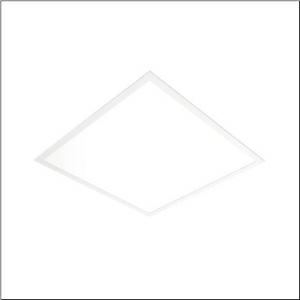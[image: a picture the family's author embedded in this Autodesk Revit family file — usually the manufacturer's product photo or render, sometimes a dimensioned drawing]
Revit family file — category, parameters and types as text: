
# Revit family: apollon_41_51mh12h72443
name_source: partatom
category: Lighting Fixtures
units: mm (PartAtom-declared; Revit-internal decimal feet)

## family parameters
Cut with Voids When Loaded = No
Host = Face
Light Source = No
Part Type = Normal
Room Calculation Point = No
Round Connector Dimension = Use Diameter
Shared = No

## types (1)
- Apollon 41 (1 x LED, 5000 lm, 38.5 W, 4000K)
    Apparent Load = 39 VA
    CIE Flux Codes = 61 87 97 100 100
    Color Rendering = 80
    Color Temperature = 4000K
    Default Elevation = 1800 mm
    Description = Apollon 41, office luminaire, primary optical cover: prismatic diffuser, of PS, light emission: direct distribution, primary light characteristic: symmetric, installation type: lay-in mounting, LED, rated luminous flux: 5.000lm, luminous efficacy: 130lm/W, light colour: 840, colour temperature: 4000K, control gear: ON/OFF, with terminal, 3-pole, mains connection: 220..240V, AC, 50/60Hz, rated input power: 38.5W, suitable for self-contained emergency lighting element 58DB00B013A with integrated self-test function according to EN 60598-2-22, housing, of aluminium section, traffic white (RAL 9016), module: M600, length: 595mm, width: 595mm, height: 60mm, recess depth: 180mm, housing upper side, of sheet steel, protection rating (complete): IP20, protection rating (lamp compartment, on room side): IP40, insulation class (complete): insulation class II (safety insulation), certification: CE, ENEC, impact resistance: IK03, permissible operating ambient temperature: -25..+40°C, packaging unit: 1 piece
    Height = 0 mm  [stored 0 ft]
    Lamp = 1 x LED
    Lamp Light Flux = 5000 lm
    Lamp Power = 38.5 W
    Lamp count = 1
    Length = 600 mm
    Luminous efficacy = 130 lm/W
    Manufacturer = Siteco
    ModVariant = No
    Model = 51MH12H72443
    Mounting Place = Ceiling
    Mounting Type = Recessed
    Number of Poles = 1
    OnlyDefault = Yes
    Power Factor = 1
    Product Name = Apollon 41
    Product group = office luminaire | ceiling recessed
    ProductGroupID = 400
    Protection Class = Protection class II
    Protection Degree = IP 20
    RLX_Detail_Level = 1
    RLX_Emergency_Light_Flux = 0 lm
    RLX_Emergency_Type = 0
    RLX_Emergency_Type_DB = No
    RlxData = <blob elided: 12433 chars, md5=7c9cb327>
    Socket = socket
    Standby Power = 0 W
    System Light Flux = 5000 lm
    System Power = 39 W
    Type Comments = Product without accessories
    Type Image = l_1291024.jpg
    URL = http://relux.com
    VarID = ---
    Voltage = 0 V
    Weight = 0.00 kg
    Width = 600 mm

note: [stored X ft] marks values corroborated as IEEE doubles in the binary element streams (Revit-internal decimal feet)

## geometry (parser evidence)
native form markers: Sweep x8
no freeform markers — native parametric forms only
